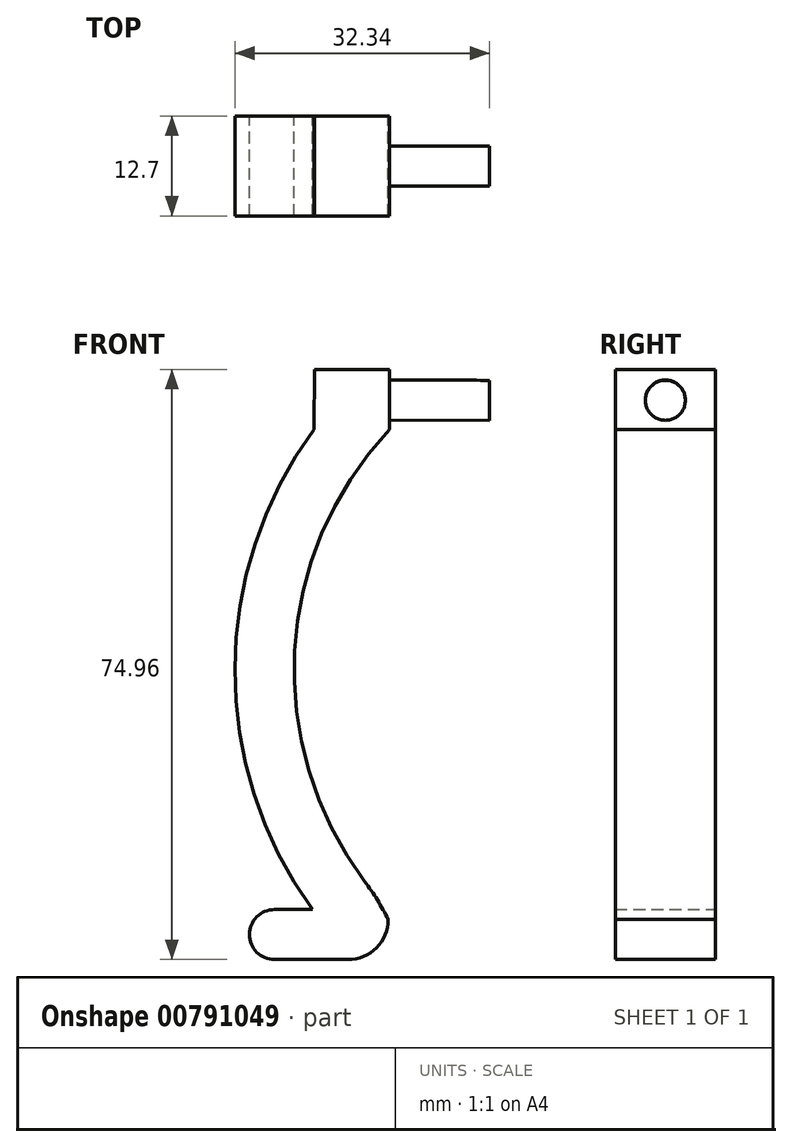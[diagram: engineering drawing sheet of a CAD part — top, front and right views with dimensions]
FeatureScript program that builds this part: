
annotation { "Feature Type Name" : "Feature", "Feature Type Description" : "" }
export const myFeature = defineFeature(function(context is Context, id is Id, definition is map)
    precondition{}
    {
        {
            var Q0;
            Q0=qCreatedBy(makeId("Front.planeOp"),FACE);
            var sketch = newSketch(context, id + "F0", { "sketchPlane" : qUnion([Q0])});
            skArc(sketch, "E0", {"start": v(-30.63, 28.63) * mm, "mid": v(-40.7, -1.83) * mm, "end": v(-30.86, -32.36) * mm});
            skArc(sketch, "E1", {"start": v(-21.08, 28.6) * mm, "mid": v(-33.15, -1.85) * mm, "end": v(-21.23, -32.36) * mm});
            skLineSegment(sketch, "E2", {"start": v(-21.08, 28.6) * mm, "end": v(-30.63, 28.63) * mm});
            skLineSegment(sketch, "E3", {"start": v(-21.23, -32.36) * mm, "end": v(-30.86, -32.36) * mm});
            skLineSegment(sketch, "E4.bottom", {"start": v(-21.23, -32.36) * mm, "end": v(-35.68, -32.36) * mm});
            skLineSegment(sketch, "E4.top", {"start": v(-21.23, -38.71) * mm, "end": v(-35.68, -38.71) * mm});
            skLineSegment(sketch, "E4.left", {"start": v(-21.23, -32.36) * mm, "end": v(-21.23, -38.71) * mm});
            skLineSegment(sketch, "E4.right", {"start": v(-35.68, -32.36) * mm, "end": v(-35.68, -38.71) * mm});
            skArc(sketch, "E5", {"start": v(-35.68, -32.36) * mm, "mid": v(-38.85, -35.54) * mm, "end": v(-35.68, -38.71) * mm});
            skSolve(sketch);
        }
        {
            var Q0;
            Q0 = qSketchRegion(id + "F0", true);
            extrude(context, id + "F1", {"entities" : qUnion([Q0]), "depth" : 12.7 * mm, "offsetDistance" : 25.4 * mm});
        }
        {
            var Q0;
            Q0=makeQuery(id+"F1.opExtrude","SWEPT_FACE",FACE,{"disambiguationData":[OSD([sQuery(id+"F0.wireOp",EDGE,"E2")])]});
            var sketch = newSketch(context, id + "F2", { "sketchPlane" : qUnion([Q0])});
            skLineSegment(sketch, "E6.bottom", {"start": v(-30.73, 0) * mm, "end": v(-21.19, 0) * mm});
            skLineSegment(sketch, "E6.top", {"start": v(-30.73, -12.7) * mm, "end": v(-21.19, -12.7) * mm});
            skLineSegment(sketch, "E6.left", {"start": v(-30.73, 0) * mm, "end": v(-30.73, -12.7) * mm});
            skLineSegment(sketch, "E6.right", {"start": v(-21.19, 0) * mm, "end": v(-21.19, -12.7) * mm});
            skSolve(sketch);
        }
        {
            var Q0;
            Q0 = qSketchRegion(id + "F2", true);
            extrude(context, id + "F3", {"entities" : qUnion([Q0]), "operationType" : NewBodyOperationType.ADD, "depth" : 7.62 * mm, "offsetDistance" : 25.4 * mm});
        }
        {
            var Q0;
            Q0=makeQuery(id+"F3.opExtrude","SWEPT_FACE",FACE,{"disambiguationData":[OSD([sQuery(id+"F2.wireOp",EDGE,"E6.right")])]});
            var sketch = newSketch(context, id + "F4", { "sketchPlane" : qUnion([Q0])});
            skCircle(sketch, "E7", {"center": v(-6.35, 32.3) * mm, "radius": 2.54 * mm});
            skSolve(sketch);
        }
        {
            var Q0;
            Q0 = qSketchRegion(id + "F4", true);
            extrude(context, id + "F5", {"entities" : qUnion([Q0]), "operationType" : NewBodyOperationType.ADD, "depth" : 12.7 * mm, "offsetDistance" : 25.4 * mm});
        }
        {
            var Q0;
            Q0=makeQuery(id+"F1.opExtrude","SWEPT_EDGE",EDGE,{"disambiguationData":[OSD([sQuery(id+"F0.wireOp",EDGE,"E4.top"),sQuery(id+"F0.wireOp",EDGE,"E4.left")])]});
            fillet(context, id + "F6", {"entities" : qUnion([Q0]), "radius" : 5.08 * mm, "tangentPropagation" : true, "allowEdgeOverflow" : false});
        }
        {
            var Q0;
            Q0=makeQuery(id+"F1.opExtrude","SWEPT_EDGE",EDGE,{"disambiguationData":[OSD([sQuery(id+"F0.wireOp",EDGE,"E1"),sQuery(id+"F0.wireOp",EDGE,"E4.bottom"),sQuery(id+"F0.wireOp",EDGE,"E4.left")])]});
            fillet(context, id + "F7", {"entities" : qUnion([Q0]), "radius" : 30.8 * mm, "tangentPropagation" : true, "allowEdgeOverflow" : false});
        }
    });
